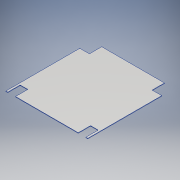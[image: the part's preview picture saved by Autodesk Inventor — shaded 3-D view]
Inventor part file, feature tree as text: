
AUTODESK INVENTOR PART (.ipt)
format: ipt  version: 2017 (Build 210142000, 142)  size: 133,120 bytes
history: native  units: mm
features: extrude x1, sketch x1
ambient origin geometry x8: Origin, YZ Plane, XZ Plane, XY Plane, X Axis, Y Axis, Z Axis, Center Point
bodies: Solid1 (feature_tree)
feature tree (2):
  extrude  "Extrusion1"  Depth=3.175mm TaperAngle=0.0deg
  sketch  "Sketch1"  dims[d0=541.02mm d1=568.96mm d2=12.7mm d6=414.02mm d10=12.7mm d11=487.68mm d14=414.02mm d17=3.175mm d18=0.0mm d19=78.105mm d20=60.325mm d22=78.105mm d23=60.325mm d26=78.105mm d27=78.105mm d28=44.45mm d29=50.8mm d30=78.105mm d31=78.105mm]
